# Revit family: Haworth_Drift32_Screen80H_EU_PRELIMINARY
name_source: partatom
category: Furniture Systems
units: mm (PartAtom-declared; Revit-internal decimal feet)

## family parameters
Always vertical = Yes
Cut with Voids When Loaded = No
OmniClass Number = 23.40.70.14.64.21
OmniClass Title = Systems Furniture
Part Type = Normal
Room Calculation Point = No
Round Connector Dimension = Use Diameter
Shared = No
Work Plane-Based = No

## types (2) — shared parameters
Actual Depth = 3.2 cm
Actual Height = 80 cm
Assembly Code = E2020200
Description = Haworth - Drift32 - 80H Screen
Manufacturer = Haworth
Model = DRS321X080
Revision Number = 1
Size = Verify Final Dim. w/ Haworth
Trim Finish = Haworth _ Metal _ Polished Aluminum
URL = https://www.haworth.com
URL - Product = https://www.haworth.com
Warranty = http://www.haworth.com
with Fixing Kit = Yes
without Fixing Kit = No

## per-type parameters (varying)
| type | Actual Width | Large | Small |
| 178.6 x 80cm | 178.6 cm | Yes | No |
| 158.6 x 80cm | 158.6 cm | No | Yes |

## geometry (parser evidence)
native form markers: Sweep x6
no freeform markers — native parametric forms only
